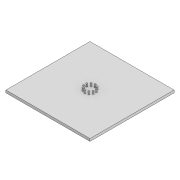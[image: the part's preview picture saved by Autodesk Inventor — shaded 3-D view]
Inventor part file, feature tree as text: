
AUTODESK INVENTOR PART (.ipt)
format: ipt  version: 2021 (Build 250183000, 183)  size: 98,816 bytes
history: native  units: in
note: dims shown in document units (in); Inventor stores cm internally (conversion verified against a paired STEP export)
features: extrude x2, sketch x2
ambient origin geometry x8: Origin, YZ Plane, XZ Plane, XY Plane, X Axis, Y Axis, Z Axis, Center Point
bodies: Solid1 (feature_tree)
feature tree (4):
  extrude  "Extrusion1"  Depth=3937.0079in
  extrude  "Extrusion2"  Depth=118.1102in
  sketch  "Sketch1"  dims[d0=3937.0079in d1=3937.0079in]
  sketch  "Sketch2"  dims[d2=118.1102in d3=0.0in d4=472.4409in d5=78.7402in d6=3.937in d8=360.0deg d10=118.1102in d11=0.0in]
